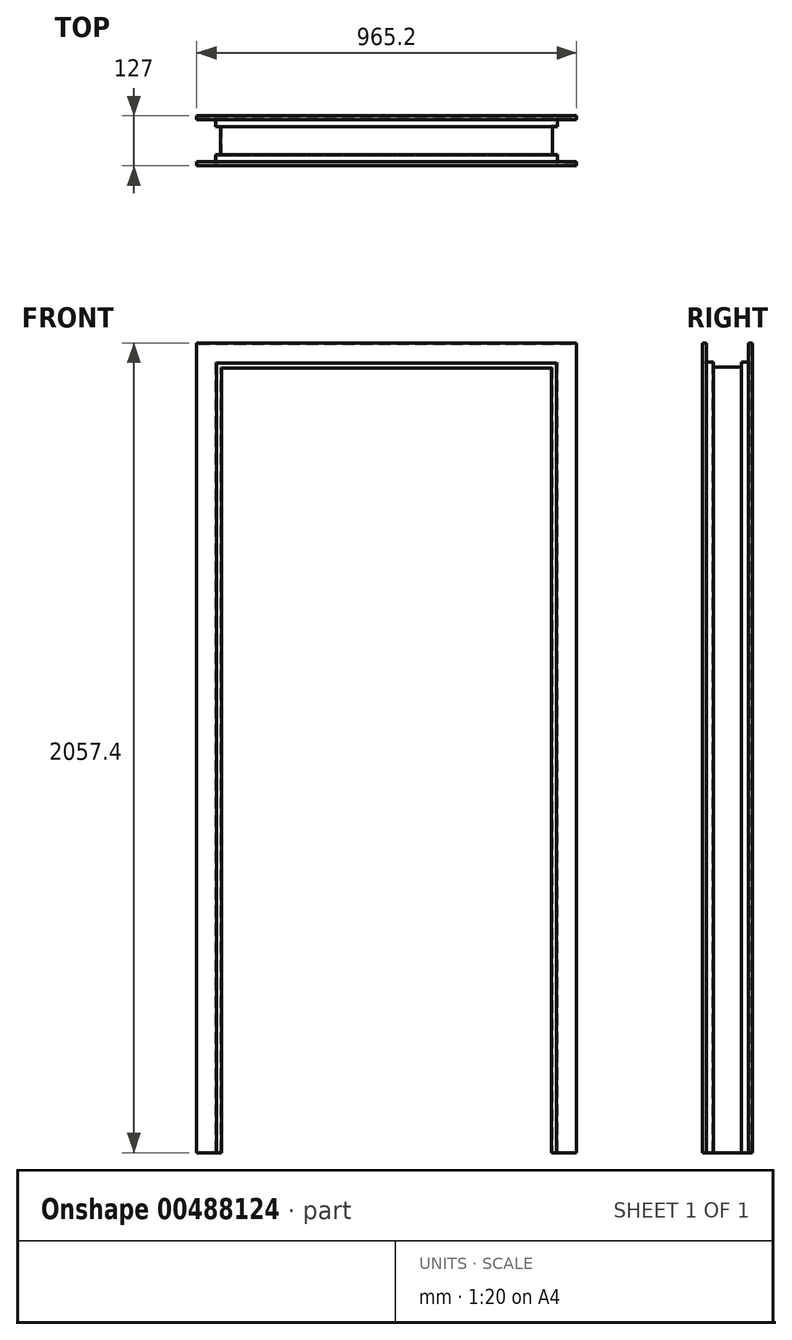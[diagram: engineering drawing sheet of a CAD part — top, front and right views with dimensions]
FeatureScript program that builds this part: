
annotation { "Feature Type Name" : "Feature", "Feature Type Description" : "" }
export const myFeature = defineFeature(function(context is Context, id is Id, definition is map)
    precondition{}
    {
        {
            var Q0;
            Q0=qCreatedBy(makeId("Top.planeOp"),FACE);
            var sketch = newSketch(context, id + "F0", { "sketchPlane" : qUnion([Q0])});
            skLineSegment(sketch, "E0", {"start": v(-25.4, 53.34) * mm, "end": v(-25.4, 63.5) * mm});
            skLineSegment(sketch, "E1", {"start": v(-25.4, 63.5) * mm, "end": v(25.4, 63.5) * mm});
            skLineSegment(sketch, "E2", {"start": v(25.4, 63.5) * mm, "end": v(25.4, 38.1) * mm});
            skLineSegment(sketch, "E3", {"start": v(25.4, 38.1) * mm, "end": v(38.1, 38.1) * mm});
            skLineSegment(sketch, "E4", {"start": v(38.1, 38.1) * mm, "end": v(38.1, -38.1) * mm});
            skLineSegment(sketch, "E5", {"start": v(38.1, -38.1) * mm, "end": v(25.4, -38.1) * mm});
            skLineSegment(sketch, "E6", {"start": v(25.4, -38.1) * mm, "end": v(25.4, -63.5) * mm});
            skLineSegment(sketch, "E7", {"start": v(25.4, -63.5) * mm, "end": v(-25.4, -63.5) * mm});
            skLineSegment(sketch, "E8", {"start": v(-25.4, -63.5) * mm, "end": v(-25.4, -53.34) * mm});
            skLineSegment(sketch, "E9", {"start": v(-25.4, -53.34) * mm, "end": v(-22.86, -53.34) * mm});
            skLineSegment(sketch, "E10", {"start": v(-22.86, -53.34) * mm, "end": v(-22.86, -60.96) * mm});
            skLineSegment(sketch, "E11", {"start": v(-22.86, -60.96) * mm, "end": v(22.86, -60.96) * mm});
            skLineSegment(sketch, "E12", {"start": v(22.86, -60.96) * mm, "end": v(22.86, -35.56) * mm});
            skLineSegment(sketch, "E13", {"start": v(22.86, -35.56) * mm, "end": v(35.56, -35.56) * mm});
            skLineSegment(sketch, "E14", {"start": v(35.56, -35.56) * mm, "end": v(35.56, 35.56) * mm});
            skLineSegment(sketch, "E15", {"start": v(35.56, 35.56) * mm, "end": v(22.86, 35.56) * mm});
            skLineSegment(sketch, "E16", {"start": v(22.86, 35.56) * mm, "end": v(22.86, 60.96) * mm});
            skLineSegment(sketch, "E17", {"start": v(22.86, 60.96) * mm, "end": v(-22.86, 60.96) * mm});
            skLineSegment(sketch, "E18", {"start": v(-22.86, 60.96) * mm, "end": v(-22.86, 53.34) * mm});
            skLineSegment(sketch, "E19", {"start": v(-22.86, 53.34) * mm, "end": v(-25.4, 53.34) * mm});
            skSolve(sketch);
        }
        {
            var Q0;
            Q0=qCreatedBy(makeId("Front.planeOp"),FACE);
            var sketch = newSketch(context, id + "F1", { "sketchPlane" : qUnion([Q0])});
            skLineSegment(sketch, "E20", {"start": v(0, 0) * mm, "end": v(0, 2032) * mm});
            skLineSegment(sketch, "E21", {"start": v(0, 2032) * mm, "end": v(914.4, 2032) * mm});
            skLineSegment(sketch, "E22", {"start": v(914.4, 2032) * mm, "end": v(914.4, 0) * mm});
            skSolve(sketch);
        }
        {
            var Q0;
            Q0=makeQuery(id+"F0.imprint","IMPRINT",FACE,{"disambiguationData":[TD([[makeQuery(id+"F0.imprint","IMPRINT",EDGE,{"derivedFrom":sQuery(id+"F0.wireOp",EDGE,"E0")}),-1.0]])]});
            var Q1;
            Q1=sQuery(id+"F1.wireOp",EDGE,"E20");
            var Q2;
            Q2=sQuery(id+"F1.wireOp",EDGE,"E21");
            var Q3;
            Q3=sQuery(id+"F1.wireOp",EDGE,"E22");
            sweep(context, id + "F2", {"profiles" : qUnion([Q0]), "path" : qUnion([Q1, Q2, Q3])});
        }
    });
